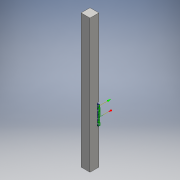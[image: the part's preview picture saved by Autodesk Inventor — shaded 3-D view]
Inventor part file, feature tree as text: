
AUTODESK INVENTOR PART (.ipt)
format: ipt  version: 2016 SP1 (Build 200210100, 210)  size: 140,800 bytes
history: native  units: mm
features: extrude x2, sketch x2
ambient origin geometry x8: Origin, YZ Plane, XZ Plane, XY Plane, X Axis, Y Axis, Z Axis, Center Point
bodies: Solid1 (feature_tree)
feature tree (4):
  extrude  "Extrusion1"  Depth=20.0mm
  extrude  "Extrusion2"  Depth=4.0mm
  sketch  "Sketch1"  dims[d0=20.0mm d1=20.0mm]
  sketch  "Sketch2"  dims[d2=10.0mm d3=10.0mm d4=300.0mm d5=0.0mm d6=47.0mm d7=80.0mm d8=4.0mm d9=0.0mm]
